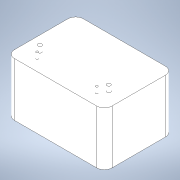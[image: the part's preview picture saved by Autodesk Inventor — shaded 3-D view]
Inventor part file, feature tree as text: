
AUTODESK INVENTOR PART (.ipt)
format: ipt  version: 2022 (Build 260153000, 153)  size: 117,760 bytes
history: native  units: in
note: dims shown in document units (in); Inventor stores cm internally (conversion verified against a paired STEP export)
features: fillet x4, extrude x2, sketch x2, mirror x1
ambient origin geometry x8: Origin, YZ Plane, XZ Plane, XY Plane, X Axis, Y Axis, Z Axis, Center Point
bodies: Solid1 (feature_tree)
feature tree (9):
  extrude  "Extrusion1"  Depth=7.0866in
  fillet  "Face Fillet1"
  fillet  "Face Fillet2"
  fillet  "Face Fillet3"
  fillet  "Face Fillet4"
  extrude  "Extrusion2"  Depth=0.7874in
  mirror  "Mirror1"
  sketch  "Sketch1"  dims[d0=10.0394in d1=7.0866in]
  sketch  "Sketch2"  dims[d2=5.5118in d3=0.0in d4=0.7874in d5=0.7874in d6=0.7874in d7=0.7874in d9=0.3937in d10=0.2362in d11=0.5906in d12=0.0in]
